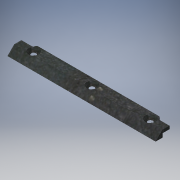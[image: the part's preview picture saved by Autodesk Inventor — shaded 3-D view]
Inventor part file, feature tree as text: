
AUTODESK INVENTOR PART (.ipt)
format: ipt  version: 2019 (Build 230136000, 136)  size: 156,160 bytes
history: native  units: mm
features: sketch x3, extrude x2, other x1, hole x1, fillet x1
ambient origin geometry x8: Origin, YZ Plane, XZ Plane, XY Plane, X Axis, Y Axis, Z Axis, Center Point
bodies: Body1 (feature_tree)
feature tree (8):
  other  "Bryła1"
  extrude  "Wyciągnięcie proste1"  Depth=11.2mm
  extrude  "Wyciągnięcie proste2"  Depth=4.5mm
  hole  "Otwór1"  [1 undecoded]
  fillet  "Zaokrąglenie1"  Radius=2.5mm
  sketch  "Szkic1"
  sketch  "Szkic2"
  sketch  "Szkic3"
note: 1 required parameter value undecoded (feature->parameter linkage not recoverable at this tier; creation-order binding heuristic only, values carry confidence <= 0.55)
